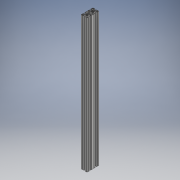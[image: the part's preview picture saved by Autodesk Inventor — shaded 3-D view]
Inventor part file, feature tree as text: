
AUTODESK INVENTOR PART (.ipt)
format: ipt  version: 2018 (Build 220112000, 112)  size: 638,976 bytes
history: native  units: mm
features: other x1, extrude x1, sketch x1
ambient origin geometry x8: Origin, YZ Plane, XZ Plane, XY Plane, X Axis, Y Axis, Z Axis, Center Point
bodies: Body1 (feature_tree)
feature tree (3):
  other  "Sólido1"
  extrude  "Extrusão1"  [1 undecoded]
  sketch  "Esboço1"  dims[d0=900.0mm d1=0.0mm]
note: 1 required parameter value undecoded (feature->parameter linkage not recoverable at this tier; creation-order binding heuristic only, values carry confidence <= 0.55)
